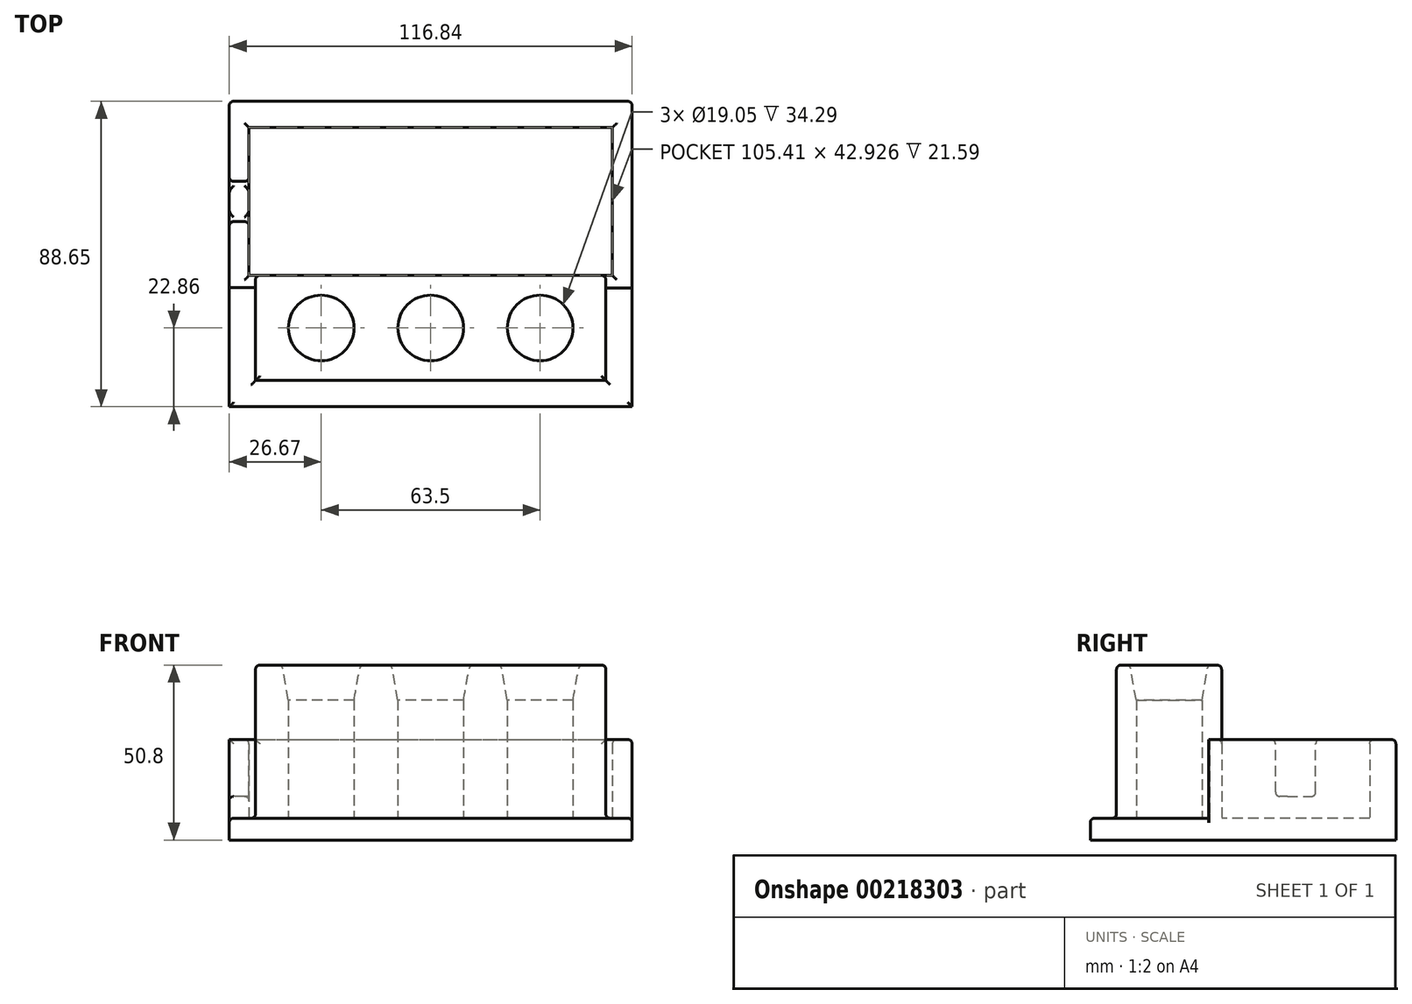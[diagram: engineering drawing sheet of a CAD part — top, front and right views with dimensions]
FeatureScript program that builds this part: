
annotation { "Feature Type Name" : "Feature", "Feature Type Description" : "" }
export const myFeature = defineFeature(function(context is Context, id is Id, definition is map)
    precondition{}
    {
        {
            var Q0;
            Q0=qCreatedBy(makeId("Top.planeOp"),FACE);
            var sketch = newSketch(context, id + "F0", { "sketchPlane" : qUnion([Q0])});
            skLineSegment(sketch, "E0.bottom", {"start": v(50.8, 15.24) * mm, "end": v(-50.8, 15.24) * mm});
            skLineSegment(sketch, "E0.top", {"start": v(50.8, -15.24) * mm, "end": v(-50.8, -15.24) * mm});
            skLineSegment(sketch, "E0.left", {"start": v(50.8, 15.24) * mm, "end": v(50.8, -15.24) * mm});
            skLineSegment(sketch, "E0.right", {"start": v(-50.8, 15.24) * mm, "end": v(-50.8, -15.24) * mm});
            skPoint(sketch, "E0.middle", {"position": v(0, 0) * mm});
            skCircle(sketch, "E1", {"center": v(0, 0) * mm, "radius": 9.53 * mm});
            skCircle(sketch, "E2", {"center": v(-31.75, 0) * mm, "radius": 9.53 * mm});
            skCircle(sketch, "E3", {"center": v(31.75, 0) * mm, "radius": 9.53 * mm});
            skSolve(sketch);
        }
        {
            var Q0;
            Q0=qSketchRegion(id+"F0",true);
            extrude(context, id + "F1", {"entities" : qUnion([Q0]), "depth" : 50.8 * mm});
        }
        {
            var Q0;
            Q0=makeQuery(id+"F0.imprint","IMPRINT",FACE,{"disambiguationData":[TD([[makeQuery(id+"F0.imprint","IMPRINT",EDGE,{"derivedFrom":sQuery(id+"F0.wireOp",EDGE,"E0.bottom")}),1.0]])]});
            var sketch = newSketch(context, id + "F2", { "sketchPlane" : qUnion([Q0])});
            skPoint(sketch, "E4.middle", {"position": v(0, 0) * mm});
            skLineSegment(sketch, "E5.bottom", {"start": v(-58.42, -22.86) * mm, "end": v(58.42, -22.86) * mm});
            skLineSegment(sketch, "E5.top", {"start": v(-58.42, 65.79) * mm, "end": v(58.42, 65.79) * mm});
            skLineSegment(sketch, "E5.left", {"start": v(-58.42, -22.86) * mm, "end": v(-58.42, 65.79) * mm});
            skLineSegment(sketch, "E5.right", {"start": v(58.42, -22.86) * mm, "end": v(58.42, 65.79) * mm});
            skLineSegment(sketch, "E6.bottom", {"start": v(-52.7, 58.17) * mm, "end": v(52.7, 58.17) * mm});
            skLineSegment(sketch, "E6.top", {"start": v(-52.7, 15.24) * mm, "end": v(52.7, 15.24) * mm});
            skLineSegment(sketch, "E6.left", {"start": v(-52.7, 58.17) * mm, "end": v(-52.7, 15.24) * mm});
            skLineSegment(sketch, "E6.right", {"start": v(52.7, 58.17) * mm, "end": v(52.7, 15.24) * mm});
            skLineSegment(sketch, "E7", {"start": v(-58.42, 11.76) * mm, "end": v(-50.8, 11.76) * mm});
            skLineSegment(sketch, "E8", {"start": v(58.42, 11.54) * mm, "end": v(50.8, 11.54) * mm});
            skSolve(sketch);
        }
        {
            var Q0;
            Q0=makeQuery(id+"F2.imprint","IMPRINT",FACE,{"disambiguationData":[TD([[makeQuery(id+"F2.imprint","IMPRINT",EDGE,{"derivedFrom":makeQuery(id+"F0.imprint","IMPRINT",EDGE,{"derivedFrom":sQuery(id+"F0.wireOp",EDGE,"E1")})}),1.0]])]});
            var Q1;
            Q1=makeQuery(id+"F2.imprint","IMPRINT",FACE,{"disambiguationData":[TD([[makeQuery(id+"F2.imprint","IMPRINT",EDGE,{"derivedFrom":makeQuery(id+"F0.imprint","IMPRINT",EDGE,{"derivedFrom":sQuery(id+"F0.wireOp",EDGE,"E2")})}),1.0]])]});
            var Q2;
            Q2=makeQuery(id+"F2.imprint","IMPRINT",FACE,{"disambiguationData":[TD([[makeQuery(id+"F2.imprint","IMPRINT",EDGE,{"derivedFrom":makeQuery(id+"F0.imprint","IMPRINT",EDGE,{"derivedFrom":sQuery(id+"F0.wireOp",EDGE,"E3")})}),1.0]])]});
            var Q3;
            {var subQ1=sQuery(id+"F2.wireOp",EDGE,"E5.bottom");Q3=makeQuery(id+"F2.imprint","IMPRINT",FACE,{"disambiguationData":[TD([[makeQuery(id+"F2.imprint","IMPRINT",EDGE,{"derivedFrom":subQ1}),1.0]])]});}
            var Q4;
            Q4=makeQuery(id+"F2.imprint","IMPRINT",FACE,{"disambiguationData":[TD([[makeQuery(id+"F2.imprint","IMPRINT",EDGE,{"derivedFrom":makeQuery(id+"F0.imprint","IMPRINT",EDGE,{"derivedFrom":sQuery(id+"F0.wireOp",EDGE,"E0.top")})}),-1.0]])]});
            var Q5;
            Q5=makeQuery(id+"F2.imprint","IMPRINT",FACE,{"disambiguationData":[TD([[makeQuery(id+"F2.imprint","IMPRINT",EDGE,{"derivedFrom":sQuery(id+"F2.wireOp",EDGE,"E6.bottom")}),-1.0]])]});
            extrude(context, id + "F3", {"entities" : qUnion([Q0, Q1, Q2, Q3, Q4, Q5]), "operationType" : NewBodyOperationType.ADD, "depth" : 6.35 * mm});
        }
        {
            var Q0;
            {var subQ2=sQuery(id+"F2.wireOp",EDGE,"E5.top");Q0=makeQuery(id+"F2.imprint","IMPRINT",FACE,{"disambiguationData":[TD([[makeQuery(id+"F2.imprint","IMPRINT",EDGE,{"derivedFrom":subQ2}),-1.0]])]});}
            extrude(context, id + "F4", {"entities" : qUnion([Q0]), "operationType" : NewBodyOperationType.ADD, "depth" : 29.2 * mm});
        }
        {
            var Q0;
            Q0=makeQuery(id+"F4.opExtrude","CAP_FACE",FACE,{"disambiguationData":[OSD([sQuery(id+"F0.wireOp",EDGE,"E0.left"),sQuery(id+"F0.wireOp",EDGE,"E0.right"),sQuery(id+"F2.wireOp",EDGE,"E5.top"),sQuery(id+"F2.wireOp",EDGE,"E5.left"),sQuery(id+"F2.wireOp",EDGE,"E5.right"),sQuery(id+"F2.wireOp",EDGE,"E6.bottom"),sQuery(id+"F2.wireOp",EDGE,"E6.top"),sQuery(id+"F2.wireOp",EDGE,"E6.left"),sQuery(id+"F2.wireOp",EDGE,"E6.right"),sQuery(id+"F2.wireOp",EDGE,"E7"),sQuery(id+"F2.wireOp",EDGE,"E8")])],"isStart":false});
            var sketch = newSketch(context, id + "F5", { "sketchPlane" : qUnion([Q0])});
            skLineSegment(sketch, "E9.bottom", {"start": v(-52.7, 42.54) * mm, "end": v(-58.42, 42.54) * mm});
            skLineSegment(sketch, "E9.top", {"start": v(-52.7, 30.86) * mm, "end": v(-58.42, 30.86) * mm});
            skLineSegment(sketch, "E9.left", {"start": v(-52.7, 42.54) * mm, "end": v(-52.7, 30.86) * mm});
            skLineSegment(sketch, "E9.right", {"start": v(-58.42, 42.54) * mm, "end": v(-58.42, 30.86) * mm});
            skSolve(sketch);
        }
        {
            var Q0;
            Q0=qSketchRegion(id+"F5",true);
            extrude(context, id + "F6", {"entities" : qUnion([Q0]), "operationType" : NewBodyOperationType.REMOVE, "oppositeDirection" : true, "depth" : 16.5 * mm});
        }
        {
            var Q0;
            Q0=makeQuery(id+"F1.opExtrude","CAP_EDGE",EDGE,{"disambiguationData":[OSD([sQuery(id+"F0.wireOp",EDGE,"E2")])],"isStart":false});
            var Q1;
            Q1=makeQuery(id+"F1.opExtrude","CAP_EDGE",EDGE,{"disambiguationData":[OSD([sQuery(id+"F0.wireOp",EDGE,"E1")])],"isStart":false});
            var Q2;
            Q2=makeQuery(id+"F1.opExtrude","CAP_EDGE",EDGE,{"disambiguationData":[OSD([sQuery(id+"F0.wireOp",EDGE,"E3")])],"isStart":false});
            chamfer(context, id + "F7", {"entities" : qUnion([Q0, Q1, Q2]), "chamferType" : ChamferType.TWO_OFFSETS, "width1" : 10.16 * mm, "oppositeDirection" : false, "width2" : 1.78 * mm, "tangentPropagation" : true});
        }
        {
            var Q0;
            {var subQ0=sQuery(id+"F0.wireOp",EDGE,"E2");Q0=makeQuery(id+"F7.opChamfer","BLEND_EDGE",EDGE,{"blendedFrom":[makeQuery(id+"F1.opExtrude","CAP_EDGE",EDGE,{"disambiguationData":[OSD([subQ0])],"isStart":false}),makeQuery(id+"F1.opExtrude","CAP_FACE",FACE,{"disambiguationData":[OSD([sQuery(id+"F0.wireOp",EDGE,"E0.bottom"),sQuery(id+"F0.wireOp",EDGE,"E0.top"),sQuery(id+"F0.wireOp",EDGE,"E0.left"),sQuery(id+"F0.wireOp",EDGE,"E0.right"),sQuery(id+"F0.wireOp",EDGE,"E1"),subQ0,sQuery(id+"F0.wireOp",EDGE,"E3")])],"isStart":false})],"blendedInto":[makeQuery(id+"F1.opExtrude","CAP_FACE",FACE,{"disambiguationData":[OSD([sQuery(id+"F0.wireOp",EDGE,"E0.bottom"),sQuery(id+"F0.wireOp",EDGE,"E0.top"),sQuery(id+"F0.wireOp",EDGE,"E0.left"),sQuery(id+"F0.wireOp",EDGE,"E0.right"),sQuery(id+"F0.wireOp",EDGE,"E1"),subQ0,sQuery(id+"F0.wireOp",EDGE,"E3")])],"isStart":false})]});}
            var Q1;
            {var subQ0=sQuery(id+"F0.wireOp",EDGE,"E1");Q1=makeQuery(id+"F7.opChamfer","BLEND_EDGE",EDGE,{"blendedFrom":[makeQuery(id+"F1.opExtrude","CAP_EDGE",EDGE,{"disambiguationData":[OSD([subQ0])],"isStart":false}),makeQuery(id+"F1.opExtrude","CAP_FACE",FACE,{"disambiguationData":[OSD([sQuery(id+"F0.wireOp",EDGE,"E0.bottom"),sQuery(id+"F0.wireOp",EDGE,"E0.top"),sQuery(id+"F0.wireOp",EDGE,"E0.left"),sQuery(id+"F0.wireOp",EDGE,"E0.right"),subQ0,sQuery(id+"F0.wireOp",EDGE,"E2"),sQuery(id+"F0.wireOp",EDGE,"E3")])],"isStart":false})],"blendedInto":[makeQuery(id+"F1.opExtrude","CAP_FACE",FACE,{"disambiguationData":[OSD([sQuery(id+"F0.wireOp",EDGE,"E0.bottom"),sQuery(id+"F0.wireOp",EDGE,"E0.top"),sQuery(id+"F0.wireOp",EDGE,"E0.left"),sQuery(id+"F0.wireOp",EDGE,"E0.right"),subQ0,sQuery(id+"F0.wireOp",EDGE,"E2"),sQuery(id+"F0.wireOp",EDGE,"E3")])],"isStart":false})]});}
            var Q2;
            {var subQ0=sQuery(id+"F0.wireOp",EDGE,"E3");Q2=makeQuery(id+"F7.opChamfer","BLEND_EDGE",EDGE,{"blendedFrom":[makeQuery(id+"F1.opExtrude","CAP_EDGE",EDGE,{"disambiguationData":[OSD([subQ0])],"isStart":false}),makeQuery(id+"F1.opExtrude","CAP_FACE",FACE,{"disambiguationData":[OSD([sQuery(id+"F0.wireOp",EDGE,"E0.bottom"),sQuery(id+"F0.wireOp",EDGE,"E0.top"),sQuery(id+"F0.wireOp",EDGE,"E0.left"),sQuery(id+"F0.wireOp",EDGE,"E0.right"),sQuery(id+"F0.wireOp",EDGE,"E1"),sQuery(id+"F0.wireOp",EDGE,"E2"),subQ0])],"isStart":false})],"blendedInto":[makeQuery(id+"F1.opExtrude","CAP_FACE",FACE,{"disambiguationData":[OSD([sQuery(id+"F0.wireOp",EDGE,"E0.bottom"),sQuery(id+"F0.wireOp",EDGE,"E0.top"),sQuery(id+"F0.wireOp",EDGE,"E0.left"),sQuery(id+"F0.wireOp",EDGE,"E0.right"),sQuery(id+"F0.wireOp",EDGE,"E1"),sQuery(id+"F0.wireOp",EDGE,"E2"),subQ0])],"isStart":false})]});}
            fillet(context, id + "F8", {"entities" : qUnion([Q0, Q1, Q2]), "radius" : 1.27 * mm, "tangentPropagation" : true, "allowEdgeOverflow" : false});
        }
        {
            var Q0;
            {var subQ0=sQuery(id+"F0.wireOp",EDGE,"E0.left");Q0=makeQuery(id+"F3.boolean.opBoolean","INTERSECT",EDGE,{"derivedFrom":[makeQuery(id+"F1.opExtrude","SWEPT_FACE",FACE,{"disambiguationData":[OSD([subQ0])]}),makeQuery(id+"F3.opExtrude","CAP_FACE",FACE,{"disambiguationData":[OSD([subQ0,sQuery(id+"F0.wireOp",EDGE,"E0.right"),sQuery(id+"F2.wireOp",EDGE,"E5.bottom"),sQuery(id+"F2.wireOp",EDGE,"E5.left"),sQuery(id+"F2.wireOp",EDGE,"E5.right"),sQuery(id+"F2.wireOp",EDGE,"E6.bottom"),sQuery(id+"F2.wireOp",EDGE,"E6.top"),sQuery(id+"F2.wireOp",EDGE,"E6.left"),sQuery(id+"F2.wireOp",EDGE,"E6.right"),sQuery(id+"F2.wireOp",EDGE,"E7"),sQuery(id+"F2.wireOp",EDGE,"E8")])],"isStart":false})]});}
            var Q1;
            Q1=makeQuery(id+"F3.boolean.opBoolean","INTERSECT",EDGE,{"derivedFrom":[makeQuery(id+"F1.opExtrude","SWEPT_FACE",FACE,{"disambiguationData":[OSD([sQuery(id+"F0.wireOp",EDGE,"E0.top")])]}),makeQuery(id+"F3.opExtrude","CAP_FACE",FACE,{"disambiguationData":[OSD([sQuery(id+"F0.wireOp",EDGE,"E0.left"),sQuery(id+"F0.wireOp",EDGE,"E0.right"),sQuery(id+"F2.wireOp",EDGE,"E5.bottom"),sQuery(id+"F2.wireOp",EDGE,"E5.left"),sQuery(id+"F2.wireOp",EDGE,"E5.right"),sQuery(id+"F2.wireOp",EDGE,"E6.bottom"),sQuery(id+"F2.wireOp",EDGE,"E6.top"),sQuery(id+"F2.wireOp",EDGE,"E6.left"),sQuery(id+"F2.wireOp",EDGE,"E6.right"),sQuery(id+"F2.wireOp",EDGE,"E7"),sQuery(id+"F2.wireOp",EDGE,"E8")])],"isStart":false})]});
            var Q2;
            {var subQ0=sQuery(id+"F0.wireOp",EDGE,"E0.right");Q2=makeQuery(id+"F3.boolean.opBoolean","INTERSECT",EDGE,{"derivedFrom":[makeQuery(id+"F1.opExtrude","SWEPT_FACE",FACE,{"disambiguationData":[OSD([subQ0])]}),makeQuery(id+"F3.opExtrude","CAP_FACE",FACE,{"disambiguationData":[OSD([sQuery(id+"F0.wireOp",EDGE,"E0.left"),subQ0,sQuery(id+"F2.wireOp",EDGE,"E5.bottom"),sQuery(id+"F2.wireOp",EDGE,"E5.left"),sQuery(id+"F2.wireOp",EDGE,"E5.right"),sQuery(id+"F2.wireOp",EDGE,"E6.bottom"),sQuery(id+"F2.wireOp",EDGE,"E6.top"),sQuery(id+"F2.wireOp",EDGE,"E6.left"),sQuery(id+"F2.wireOp",EDGE,"E6.right"),sQuery(id+"F2.wireOp",EDGE,"E7"),sQuery(id+"F2.wireOp",EDGE,"E8")])],"isStart":false})]});}
            var Q3;
            Q3=makeQuery(id+"F3.opExtrude","CAP_EDGE",EDGE,{"disambiguationData":[OSD([sQuery(id+"F2.wireOp",EDGE,"E7")])],"isStart":false});
            var Q4;
            Q4=makeQuery(id+"F4.opExtrude","SWEPT_EDGE",EDGE,{"disambiguationData":[OSD([sQuery(id+"F0.wireOp",EDGE,"E0.right"),sQuery(id+"F2.wireOp",EDGE,"E7")])]});
            var Q5;
            Q5=makeQuery(id+"F3.opExtrude","CAP_EDGE",EDGE,{"disambiguationData":[OSD([sQuery(id+"F2.wireOp",EDGE,"E8")])],"isStart":false});
            var Q6;
            Q6=makeQuery(id+"F4.opExtrude","SWEPT_EDGE",EDGE,{"disambiguationData":[OSD([sQuery(id+"F0.wireOp",EDGE,"E0.left"),sQuery(id+"F2.wireOp",EDGE,"E8")])]});
            fillet(context, id + "F9", {"entities" : qUnion([Q0, Q1, Q2, Q3, Q4, Q5, Q6]), "radius" : 1.27 * mm, "tangentPropagation" : true, "allowEdgeOverflow" : false});
        }
        {
            var Q0;
            Q0=makeQuery(id+"F3.opExtrude","CAP_EDGE",EDGE,{"disambiguationData":[OSD([sQuery(id+"F2.wireOp",EDGE,"E5.bottom")])],"isStart":false});
            var Q1;
            Q1=makeQuery(id+"F3.opExtrude","CAP_EDGE",EDGE,{"disambiguationData":[OSD([sQuery(id+"F2.wireOp",EDGE,"E5.right")])],"isStart":false});
            var Q2;
            Q2=makeQuery(id+"F1.opExtrude","CAP_EDGE",EDGE,{"disambiguationData":[OSD([sQuery(id+"F0.wireOp",EDGE,"E0.left")])],"isStart":false});
            var Q3;
            Q3=makeQuery(id+"F1.opExtrude","CAP_EDGE",EDGE,{"disambiguationData":[OSD([sQuery(id+"F0.wireOp",EDGE,"E0.top")])],"isStart":false});
            var Q4;
            Q4=makeQuery(id+"F3.opExtrude","CAP_EDGE",EDGE,{"disambiguationData":[OSD([sQuery(id+"F2.wireOp",EDGE,"E5.left")])],"isStart":false});
            var Q5;
            Q5=makeQuery(id+"F1.opExtrude","CAP_EDGE",EDGE,{"disambiguationData":[OSD([sQuery(id+"F0.wireOp",EDGE,"E0.right")])],"isStart":false});
            var Q6;
            Q6=makeQuery(id+"F1.opExtrude","CAP_EDGE",EDGE,{"disambiguationData":[OSD([sQuery(id+"F0.wireOp",EDGE,"E0.bottom")])],"isStart":false});
            var Q7;
            Q7=makeQuery(id+"F3.boolean.opBoolean","SPLIT",EDGE,{"derivedFrom":makeQuery(id+"F1.opExtrude","SWEPT_EDGE",EDGE,{"disambiguationData":[OSD([sQuery(id+"F0.wireOp",EDGE,"E0.bottom"),sQuery(id+"F0.wireOp",EDGE,"E0.right")])]})});
            var Q8;
            Q8=makeQuery(id+"F3.boolean.opBoolean","SPLIT",EDGE,{"derivedFrom":makeQuery(id+"F1.opExtrude","SWEPT_EDGE",EDGE,{"disambiguationData":[OSD([sQuery(id+"F0.wireOp",EDGE,"E0.bottom"),sQuery(id+"F0.wireOp",EDGE,"E0.left")])]})});
            fillet(context, id + "F10", {"entities" : qUnion([Q0, Q1, Q2, Q3, Q4, Q5, Q6, Q7, Q8]), "radius" : 1.27 * mm, "tangentPropagation" : true, "allowEdgeOverflow" : false});
        }
        {
            var Q0;
            Q0=makeQuery(id+"F4.opExtrude","CAP_EDGE",EDGE,{"disambiguationData":[OSD([sQuery(id+"F2.wireOp",EDGE,"E6.right")])],"isStart":false});
            var Q1;
            {var subQ0=sQuery(id+"F2.wireOp",EDGE,"E6.top");Q1=makeQuery(id+"F4.opExtrude","CAP_EDGE",EDGE,{"disambiguationData":[OSD([subQ0]),TDD([makeQuery(id+"F2.imprint","IMPRINT",EDGE,{"disambiguationData":[TD([[makeQuery(id+"F2.imprint","INTERSECT",VERTEX,{"derivedFrom":[makeQuery(id+"F0.imprint","IMPRINT",EDGE,{"derivedFrom":sQuery(id+"F0.wireOp",EDGE,"E0.left")}),subQ0]}),-1.0],[makeQuery(id+"F2.imprint","INTERSECT",VERTEX,{"derivedFrom":[subQ0,sQuery(id+"F2.wireOp",EDGE,"E6.right")]}),1.0]])],"derivedFrom":subQ0})])],"isStart":false});}
            var Q2;
            {var subQ0=sQuery(id+"F2.wireOp",EDGE,"E6.top");Q2=makeQuery(id+"F4.opExtrude","CAP_EDGE",EDGE,{"disambiguationData":[OSD([subQ0]),TDD([makeQuery(id+"F2.imprint","IMPRINT",EDGE,{"disambiguationData":[TD([[makeQuery(id+"F2.imprint","INTERSECT",VERTEX,{"derivedFrom":[makeQuery(id+"F0.imprint","IMPRINT",EDGE,{"derivedFrom":sQuery(id+"F0.wireOp",EDGE,"E0.right")}),subQ0]}),1.0],[makeQuery(id+"F2.imprint","INTERSECT",VERTEX,{"derivedFrom":[subQ0,sQuery(id+"F2.wireOp",EDGE,"E6.left")]}),-1.0]])],"derivedFrom":subQ0})])],"isStart":false});}
            var Q3;
            {var subQ4=sQuery(id+"F2.wireOp",EDGE,"E6.left");Q3=makeQuery(id+"F6.boolean.opBoolean","SPLIT",EDGE,{"disambiguationData":[TD([makeQuery(id+"F1.opExtrude","SWEPT_FACE",FACE,{"disambiguationData":[OSD([sQuery(id+"F0.wireOp",EDGE,"E0.bottom")])]})])],"derivedFrom":makeQuery(id+"F4.opExtrude","CAP_EDGE",EDGE,{"disambiguationData":[OSD([subQ4])],"isStart":false})});}
            var Q4;
            {var subQ0=sQuery(id+"F2.wireOp",EDGE,"E6.left");var subQ1=sQuery(id+"F2.wireOp",EDGE,"E6.bottom");Q4=makeQuery(id+"F6.boolean.opBoolean","SPLIT",EDGE,{"disambiguationData":[TD([makeQuery(id+"F4.opExtrude","SWEPT_FACE",FACE,{"disambiguationData":[OSD([subQ1])]})])],"derivedFrom":makeQuery(id+"F4.opExtrude","CAP_EDGE",EDGE,{"disambiguationData":[OSD([subQ0])],"isStart":false})});}
            var Q5;
            Q5=makeQuery(id+"F4.opExtrude","CAP_EDGE",EDGE,{"disambiguationData":[OSD([sQuery(id+"F2.wireOp",EDGE,"E6.bottom")])],"isStart":false});
            var Q6;
            Q6=makeQuery(id+"F6.boolean.opBoolean","COPY",FACE,{"derivedFrom":makeQuery(id+"F6.opExtrude","SWEPT_FACE",FACE,{"disambiguationData":[OSD([sQuery(id+"F5.wireOp",EDGE,"E9.top")])]})});
            var Q7;
            Q7=makeQuery(id+"F6.boolean.opBoolean","COPY",FACE,{"derivedFrom":makeQuery(id+"F6.opExtrude","SWEPT_FACE",FACE,{"disambiguationData":[OSD([sQuery(id+"F5.wireOp",EDGE,"E9.bottom")])]})});
            var Q8;
            Q8=makeQuery(id+"F4.opExtrude","SWEPT_EDGE",EDGE,{"disambiguationData":[OSD([sQuery(id+"F2.wireOp",EDGE,"E5.top"),sQuery(id+"F2.wireOp",EDGE,"E5.left")])]});
            var Q9;
            {var subQ0=sQuery(id+"F2.wireOp",EDGE,"E5.left");var subQ1=sQuery(id+"F2.wireOp",EDGE,"E5.top");Q9=makeQuery(id+"F6.boolean.opBoolean","SPLIT",EDGE,{"disambiguationData":[TD([makeQuery(id+"F4.opExtrude","SWEPT_FACE",FACE,{"disambiguationData":[OSD([subQ1])]})])],"derivedFrom":makeQuery(id+"F4.opExtrude","CAP_EDGE",EDGE,{"disambiguationData":[OSD([subQ0])],"isStart":false})});}
            var Q10;
            Q10=makeQuery(id+"F4.opExtrude","CAP_EDGE",EDGE,{"disambiguationData":[OSD([sQuery(id+"F2.wireOp",EDGE,"E5.top")])],"isStart":false});
            var Q11;
            Q11=makeQuery(id+"F4.opExtrude","CAP_EDGE",EDGE,{"disambiguationData":[OSD([sQuery(id+"F2.wireOp",EDGE,"E5.right")])],"isStart":false});
            var Q12;
            Q12=makeQuery(id+"F4.opExtrude","SWEPT_EDGE",EDGE,{"disambiguationData":[OSD([sQuery(id+"F2.wireOp",EDGE,"E5.top"),sQuery(id+"F2.wireOp",EDGE,"E5.right")])]});
            fillet(context, id + "F11", {"entities" : qUnion([Q0, Q1, Q2, Q3, Q4, Q5, Q6, Q7, Q8, Q9, Q10, Q11, Q12]), "radius" : 1.27 * mm, "tangentPropagation" : true, "allowEdgeOverflow" : false});
        }
    });
